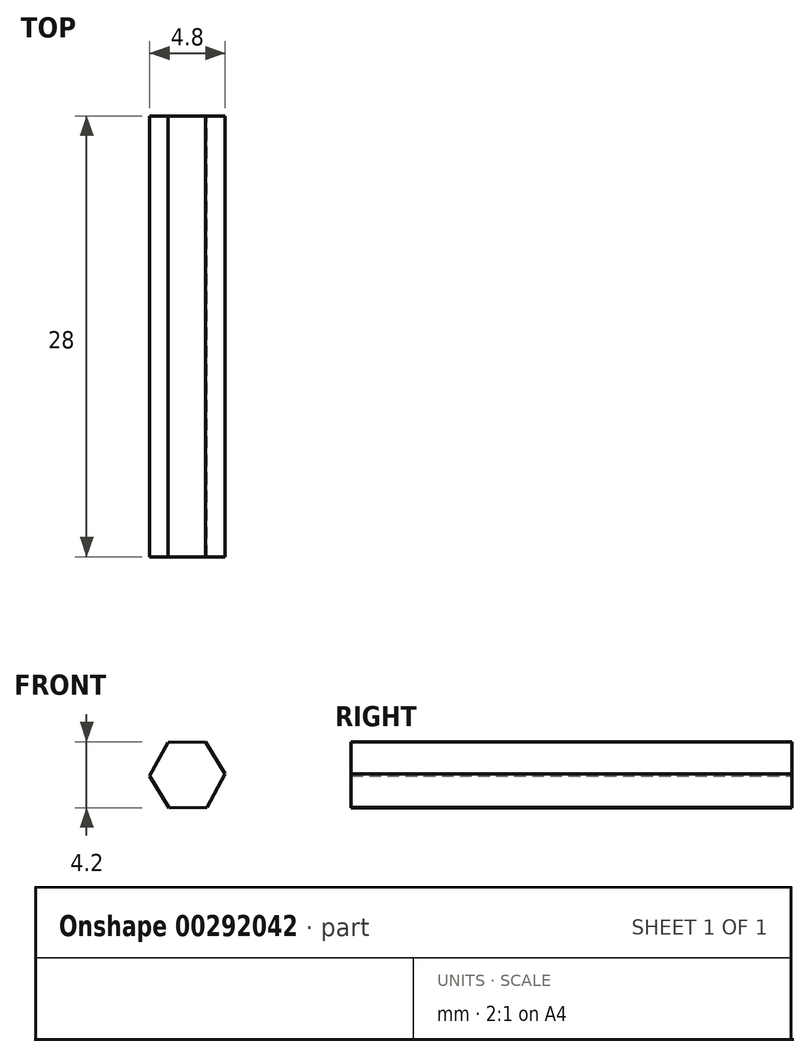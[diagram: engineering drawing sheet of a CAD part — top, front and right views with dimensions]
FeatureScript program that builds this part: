
annotation { "Feature Type Name" : "Feature", "Feature Type Description" : "" }
export const myFeature = defineFeature(function(context is Context, id is Id, definition is map)
    precondition{}
    {
        {
            var Q0;
            Q0=qCreatedBy(makeId("Front.planeOp"),FACE);
            var sketch = newSketch(context, id + "F0", { "sketchPlane" : qUnion([Q0])});
            skCircle(sketch, "E0.cCircle", {"center": v(0, 0) * mm, "radius": 2.08 * mm, "construction": true});
            skLineSegment(sketch, "E0.0", {"start": v(1.15, 2.1) * mm, "end": v(2.4, 0.05) * mm});
            skLineSegment(sketch, "E0.1", {"start": v(2.4, 0.05) * mm, "end": v(1.25, -2.05) * mm});
            skLineSegment(sketch, "E0.2", {"start": v(1.25, -2.05) * mm, "end": v(-1.15, -2.1) * mm});
            skLineSegment(sketch, "E0.3", {"start": v(-1.15, -2.1) * mm, "end": v(-2.4, -0.05) * mm});
            skLineSegment(sketch, "E0.4", {"start": v(-2.4, -0.05) * mm, "end": v(-1.25, 2.05) * mm});
            skLineSegment(sketch, "E0.5", {"start": v(-1.25, 2.05) * mm, "end": v(1.15, 2.1) * mm});
            skPoint(sketch, "E0.0.midPoint", {"position": v(1.78, 1.08) * mm});
            skSolve(sketch);
        }
        {
            var Q0;
            Q0 = qSketchRegion(id + "F0", true);
            extrude(context, id + "F1", {"entities" : qUnion([Q0]), "depth" : 28 * mm});
        }
    });
